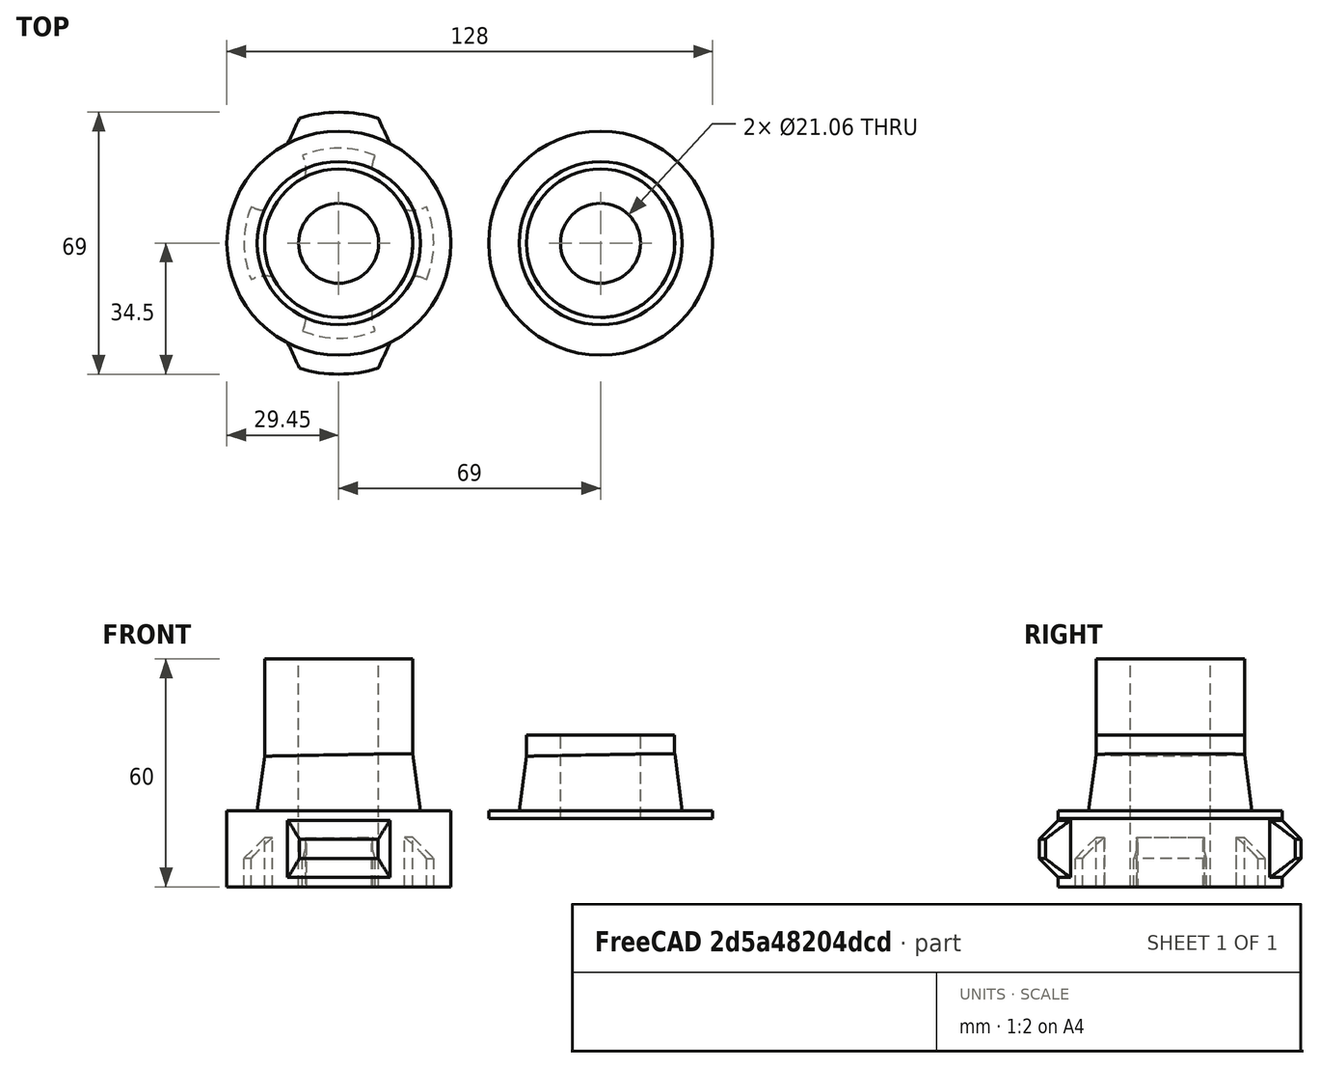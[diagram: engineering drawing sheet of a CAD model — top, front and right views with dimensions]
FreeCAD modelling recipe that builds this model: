
FCSTD DOCUMENT  (FreeCAD 0.17R13522 (Git))
Label: fat_mounting
License: CreativeCommons Attribution-ShareAlike
LicenseURL: http://creativecommons.org/licenses/by-sa/4.0/
objects: Part::Cut×4, Part::Box×3, Part::Feature×2, Part::Cylinder×2, Part::MultiFuse×1
note: 12 computed .brp shape members not serialized (recipe doc carries the construction recipe); baked Part::Feature solids carry a one-line shape summary decoded from their .brp

FEATURE [Part::Feature] Part__Feature  label="Bolzen"
  shape: bbox 59 x 69 x 35 mm, 40 faces (baked)
FEATURE [Part::Cylinder] Cylinder
  Angle = 360
  AttacherType = Attacher::AttachEngine3D
  Height = 90
  Placement = pos=(-0.05,0,0) rot=(0,0,1;0rad)
  Radius = 19.53
FEATURE [Part::Cylinder] Cylinder001
  Angle = 360
  AttacherType = Attacher::AttachEngine3D
  Height = 100
  Placement = pos=(-0.05,0,-5) rot=(0,0,1;0rad)
  Radius = 10.53
FEATURE [Part::MultiFuse] Fusion
  Shapes = -> [Part__Feature,Cylinder]
FEATURE [Part::Cut] Cut
  Base = -> Fusion
  Tool = -> Cylinder001
FEATURE [Part::Feature] Cut001
  Placement = pos=(69,0,0) rot=(0,0,1;0rad)
  shape: bbox 59 x 69 x 90 mm, 52 faces (baked)
FEATURE [Part::Box] Box  label="Cube"
  AttacherType = Attacher::AttachEngine3D
  Height = 18
  Length = 70
  Placement = pos=(35,-41,0) rot=(0,0,1;0rad)
  Width = 80
FEATURE [Part::Box] Box001  label="Cube001"
  AttacherType = Attacher::AttachEngine3D
  Height = 61
  Length = 70
  Placement = pos=(35,-41,40) rot=(0,0,1;0rad)
  Width = 80
FEATURE [Part::Cut] Cut002
  Base = -> Cut001
  Tool = -> Box
FEATURE [Part::Cut] Cut003
  Base = -> Cut002
  Tool = -> Box001
FEATURE [Part::Box] Box002  label="Cube002"
  AttacherType = Attacher::AttachEngine3D
  Height = 43
  Length = 70
  Placement = pos=(-36,-41,60) rot=(0,0,1;0rad)
  Width = 80
FEATURE [Part::Cut] Cut004
  Base = -> Cut
  Tool = -> Box002
